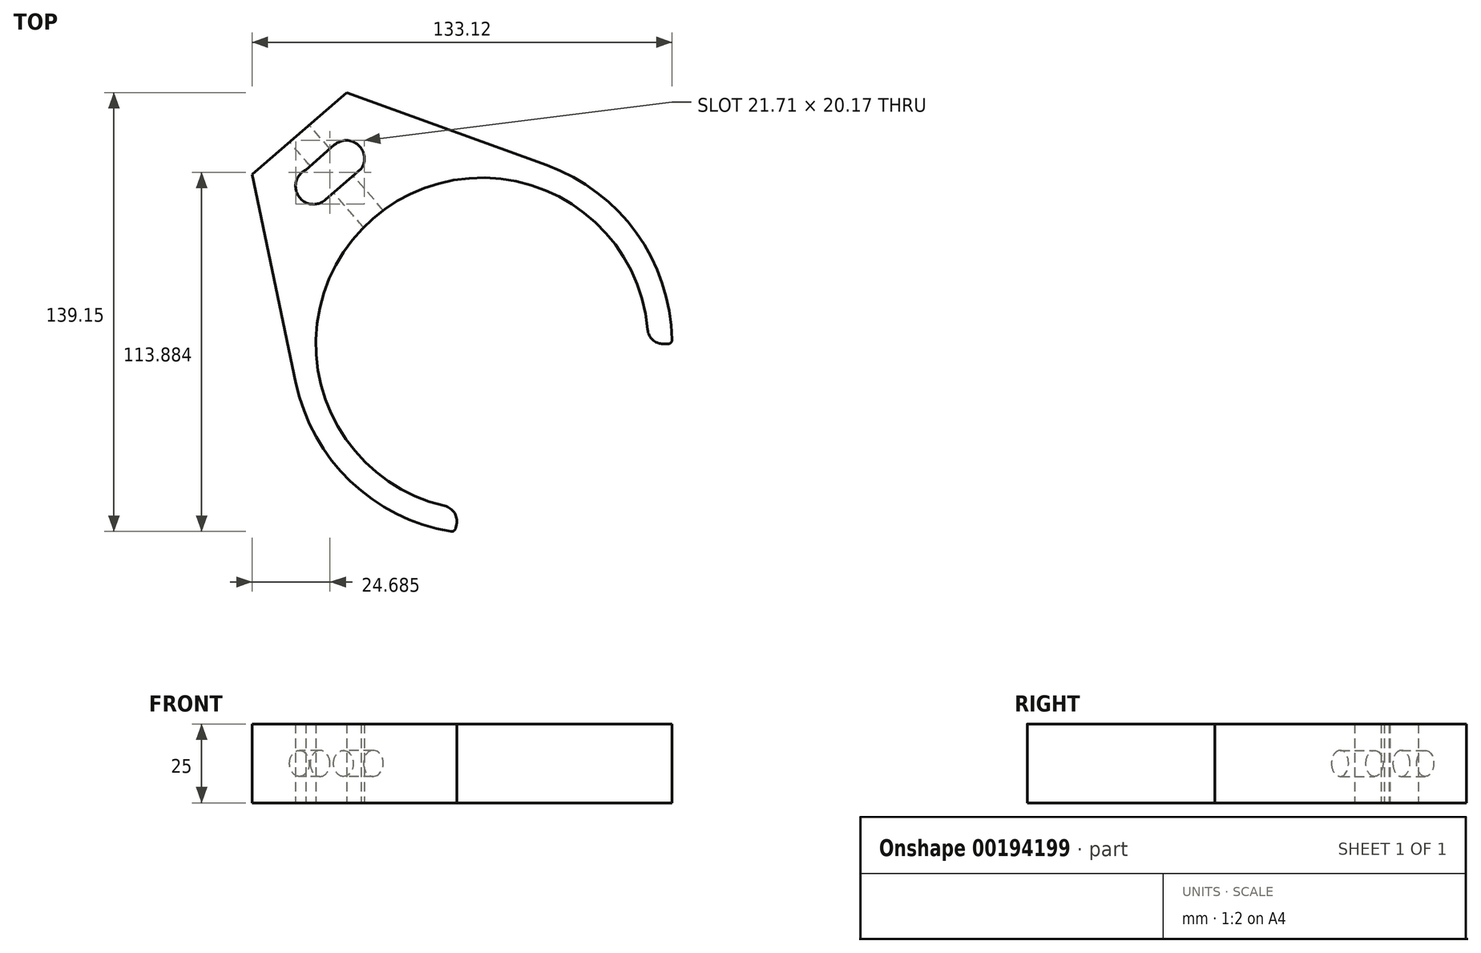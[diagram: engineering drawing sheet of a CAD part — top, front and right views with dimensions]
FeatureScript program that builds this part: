
annotation { "Feature Type Name" : "Feature", "Feature Type Description" : "" }
export const myFeature = defineFeature(function(context is Context, id is Id, definition is map)
    precondition{}
    {
        {
            var Q0;
            Q0=qCreatedBy(makeId("Top.planeOp"),FACE);
            var sketch = newSketch(context, id + "F0", { "sketchPlane" : qUnion([Q0])});
            skArc(sketch, "E0", {"start": v(52.48, 4.57) * mm, "mid": v(-34.54, 39.77) * mm, "end": v(-11.87, -51.32) * mm});
            skArc(sketch, "E1", {"start": v(60.25, 1.4) * mm, "mid": v(-39.49, 45.53) * mm, "end": v(-9.92, -59.45) * mm});
            skLineSegment(sketch, "E2", {"start": v(57.46, 0) * mm, "end": v(58.88, 0) * mm});
            skLineSegment(sketch, "E3", {"start": v(-8.35, -58.38) * mm, "end": v(-8.1, -57.21) * mm});
            skPoint(sketch, "E4.visualSharp", {"position": v(52.67, 0) * mm});
            skArc(sketch, "E4.filletArc", {"start": v(52.48, 4.57) * mm, "mid": v(54.08, 1.31) * mm, "end": v(57.46, 0) * mm});
            skPoint(sketch, "E5.visualSharp", {"position": v(60.27, 0) * mm});
            skArc(sketch, "E5.filletArc", {"start": v(58.88, 0) * mm, "mid": v(59.86, 0.41) * mm, "end": v(60.25, 1.4) * mm});
            skPoint(sketch, "E6.visualSharp", {"position": v(-8.62, -59.65) * mm});
            skArc(sketch, "E6.filletArc", {"start": v(-9.92, -59.45) * mm, "mid": v(-8.92, -59.23) * mm, "end": v(-8.35, -58.38) * mm});
            skPoint(sketch, "E7.visualSharp", {"position": v(-7.06, -52.2) * mm});
            skArc(sketch, "E7.filletArc", {"start": v(-8.1, -57.21) * mm, "mid": v(-8.79, -53.5) * mm, "end": v(-11.87, -51.32) * mm});
            skLineSegment(sketch, "E8", {"start": v(-11.87, -51.32) * mm, "end": v(52.48, 4.57) * mm, "construction": true});
            skLineSegment(sketch, "E9", {"start": v(20.3, -23.38) * mm, "end": v(-57.91, 66.68) * mm, "construction": true});
            skLineSegment(sketch, "E10", {"start": v(-57.91, 66.68) * mm, "end": v(-42.95, 79.68) * mm});
            skLineSegment(sketch, "E11", {"start": v(-42.95, 79.68) * mm, "end": v(-22.36, 55.97) * mm});
            skLineSegment(sketch, "E12", {"start": v(-57.91, 66.68) * mm, "end": v(-72.87, 53.68) * mm});
            skLineSegment(sketch, "E13", {"start": v(-72.87, 53.68) * mm, "end": v(-52.29, 29.98) * mm});
            skLineSegment(sketch, "E14", {"start": v(-51.35, 59.13) * mm, "end": v(-55.91, 55.17) * mm});
            skLineSegment(sketch, "E15.MirrorCS", {"start": v(-51.35, 59.13) * mm, "end": v(-46.8, 63.1) * mm});
            skLineSegment(sketch, "E16", {"start": v(-43.95, 50.6) * mm, "end": v(-49.6, 45.69) * mm});
            skLineSegment(sketch, "E17.MirrorCS", {"start": v(-43.95, 50.6) * mm, "end": v(-38.28, 55.52) * mm});
            skArc(sketch, "E18", {"start": v(-49.6, 45.69) * mm, "mid": v(-58.16, 46.84) * mm, "end": v(-55.91, 55.17) * mm});
            skArc(sketch, "E19", {"start": v(-46.8, 63.1) * mm, "mid": v(-39.21, 63.05) * mm, "end": v(-38.28, 55.52) * mm});
            skLineSegment(sketch, "E20", {"start": v(-72.87, 53.68) * mm, "end": v(-58.98, -12.4) * mm});
            skLineSegment(sketch, "E21", {"start": v(-42.95, 79.68) * mm, "end": v(20.54, 56.66) * mm});
            skSolve(sketch);
        }
        {
            var Q0;
            Q0 = qSketchRegion(id + "F0", true);
            extrude(context, id + "F1", {"entities" : qUnion([Q0]), "depth" : 25 * mm});
        }
        {
            var Q0;
            Q0=makeQuery(id+"F1.opExtrude","SWEPT_FACE",FACE,{"disambiguationData":[OSD([sQuery(id+"F0.wireOp",EDGE,"E10"),sQuery(id+"F0.wireOp",EDGE,"E12")])]});
            var sketch = newSketch(context, id + "F2", { "sketchPlane" : qUnion([Q0])});
            skCircle(sketch, "E22", {"center": v(0, 12.5) * mm, "radius": 4.13 * mm});
            skPoint(sketch, "E22.centerSnap0", {"position": v(19.82, 12.5) * mm});
            skSolve(sketch);
        }
        {
            var Q0;
            Q0 = qSketchRegion(id + "F2", true);
            extrude(context, id + "F3", {"entities" : qUnion([Q0]), "operationType" : NewBodyOperationType.REMOVE, "oppositeDirection" : true, "depth" : 100 * mm});
        }
    });
